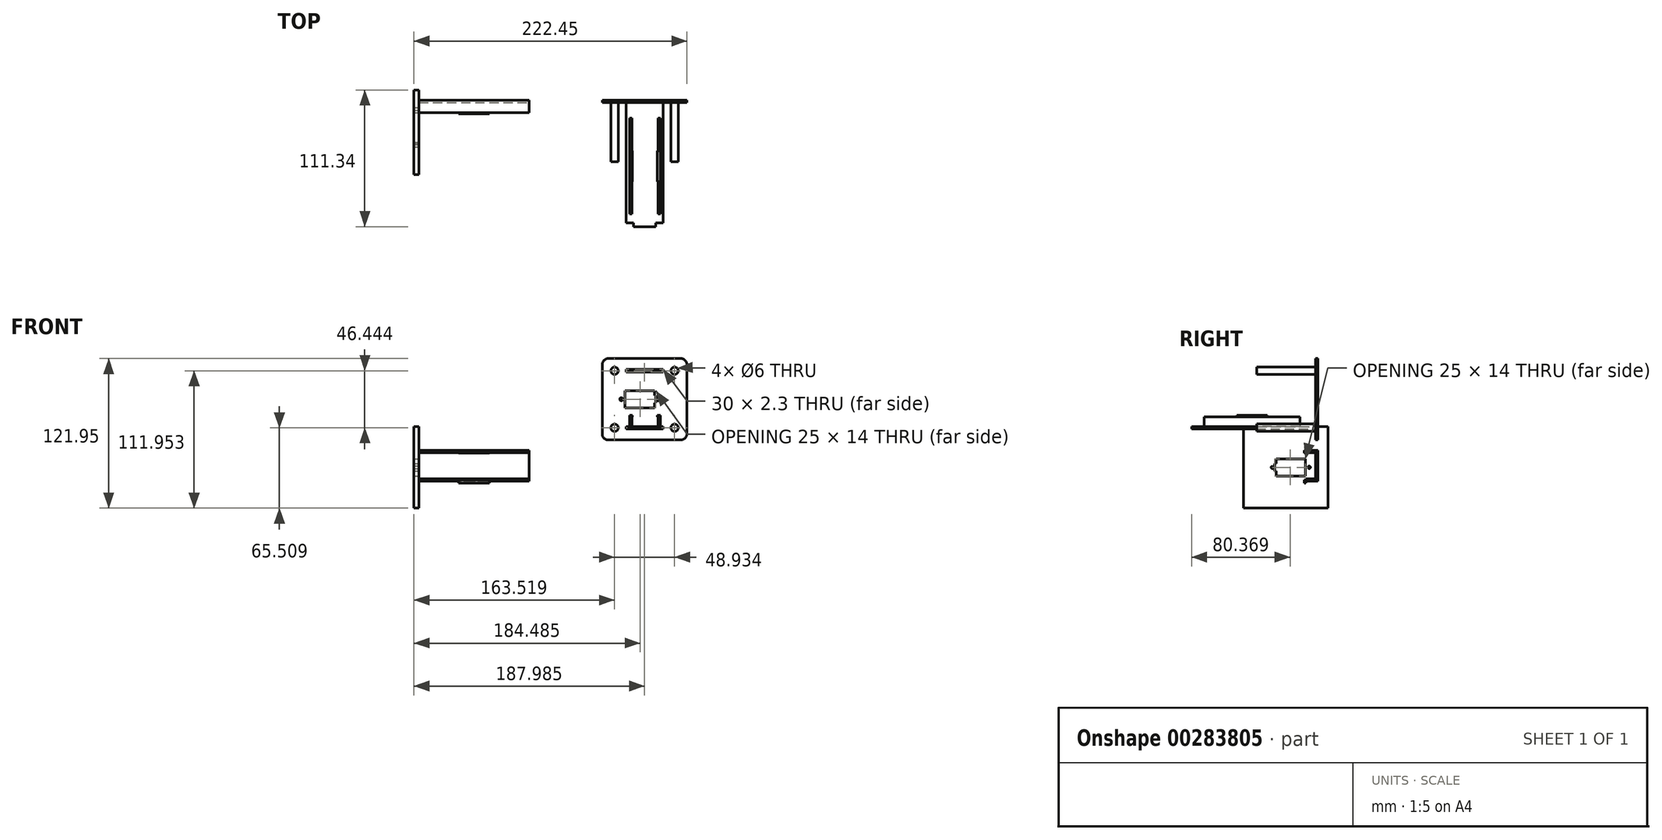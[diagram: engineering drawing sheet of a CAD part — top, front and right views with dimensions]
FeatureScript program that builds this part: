
annotation { "Feature Type Name" : "Feature", "Feature Type Description" : "" }
export const myFeature = defineFeature(function(context is Context, id is Id, definition is map)
    precondition{}
    {
        {
            var Q0;
            Q0=qCreatedBy(makeId("Front.planeOp"),FACE);
            var sketch = newSketch(context, id + "F0", { "sketchPlane" : qUnion([Q0])});
            skLineSegment(sketch, "E0.bottom", {"start": v(-132.32, 48.21) * mm, "end": v(-201.25, 48.21) * mm});
            skLineSegment(sketch, "E0.top", {"start": v(-132.32, -18.23) * mm, "end": v(-201.25, -18.23) * mm});
            skLineSegment(sketch, "E0.left", {"start": v(-132.32, 48.21) * mm, "end": v(-132.32, -18.23) * mm});
            skLineSegment(sketch, "E0.right", {"start": v(-201.25, 48.21) * mm, "end": v(-201.25, -18.23) * mm});
            skLineSegment(sketch, "E1.bottom", {"start": v(-158.78, 22) * mm, "end": v(-182.78, 22) * mm});
            skLineSegment(sketch, "E1.top", {"start": v(-158.78, 8) * mm, "end": v(-182.78, 8) * mm});
            skLineSegment(sketch, "E1.left", {"start": v(-158.78, 22) * mm, "end": v(-158.78, 8) * mm});
            skLineSegment(sketch, "E1.right", {"start": v(-182.78, 22) * mm, "end": v(-182.78, 8) * mm});
            skLineSegment(sketch, "E2.bottom", {"start": v(-157.78, 18) * mm, "end": v(-158.78, 18) * mm});
            skLineSegment(sketch, "E2.top", {"start": v(-157.78, 12) * mm, "end": v(-158.78, 12) * mm});
            skLineSegment(sketch, "E2.left", {"start": v(-157.78, 18) * mm, "end": v(-157.78, 12) * mm});
            skLineSegment(sketch, "E2.right", {"start": v(-158.78, 18) * mm, "end": v(-158.78, 12) * mm});
            skCircle(sketch, "E3", {"center": v(-155.78, 15) * mm, "radius": 1.25 * mm});
            skCircle(sketch, "E4", {"center": v(-185.78, 15) * mm, "radius": 1.25 * mm});
            skPoint(sketch, "E5", {"position": v(-182.78, 15) * mm});
            skPoint(sketch, "E6", {"position": v(-157.78, 15) * mm});
            skPoint(sketch, "E7", {"position": v(-158.78, 15) * mm});
            skPoint(sketch, "E8", {"position": v(-166.78, 48.21) * mm});
            skPoint(sketch, "E9", {"position": v(-132.32, 15) * mm});
            skPoint(sketch, "E10", {"position": v(-201.25, 15) * mm});
            skPoint(sketch, "E11", {"position": v(-166.78, -18.23) * mm});
            skLineSegment(sketch, "E12", {"start": v(-105.7, 15) * mm, "end": v(-235.07, 15) * mm, "construction": true});
            skPoint(sketch, "E13", {"position": v(-166.78, 22) * mm});
            skLineSegment(sketch, "E14.bottom", {"start": v(-350.77, -28.53) * mm, "end": v(-260.77, -28.53) * mm});
            skLineSegment(sketch, "E14.top", {"start": v(-350.77, -49.78) * mm, "end": v(-260.77, -49.78) * mm});
            skLineSegment(sketch, "E14.left", {"start": v(-350.77, -28.53) * mm, "end": v(-350.77, -49.78) * mm});
            skLineSegment(sketch, "E14.right", {"start": v(-260.77, -28.53) * mm, "end": v(-260.77, -49.78) * mm});
            skCircle(sketch, "E15", {"center": v(-191.25, 38.21) * mm, "radius": 3 * mm});
            skCircle(sketch, "E16", {"center": v(-142.32, 38.21) * mm, "radius": 3 * mm});
            skCircle(sketch, "E17", {"center": v(-142.32, -8.23) * mm, "radius": 3 * mm});
            skCircle(sketch, "E18", {"center": v(-191.25, -8.23) * mm, "radius": 3 * mm});
            skLineSegment(sketch, "E19.top", {"start": v(-350.77, -26.53) * mm, "end": v(-260.77, -26.53) * mm});
            skLineSegment(sketch, "E19.left", {"start": v(-350.77, -28.53) * mm, "end": v(-350.77, -26.53) * mm});
            skLineSegment(sketch, "E19.right", {"start": v(-260.77, -28.53) * mm, "end": v(-260.77, -26.53) * mm});
            skLineSegment(sketch, "E20.bottom", {"start": v(-260.77, -49.78) * mm, "end": v(-350.77, -49.78) * mm});
            skLineSegment(sketch, "E20.top", {"start": v(-260.77, -51.78) * mm, "end": v(-350.77, -51.78) * mm});
            skLineSegment(sketch, "E20.left", {"start": v(-260.77, -49.78) * mm, "end": v(-260.77, -51.78) * mm});
            skLineSegment(sketch, "E20.right", {"start": v(-350.77, -49.78) * mm, "end": v(-350.77, -51.78) * mm});
            skLineSegment(sketch, "E21.bottom", {"start": v(-151.78, 37.06) * mm, "end": v(-181.78, 37.06) * mm});
            skLineSegment(sketch, "E21.top", {"start": v(-151.78, 39.36) * mm, "end": v(-181.78, 39.36) * mm});
            skLineSegment(sketch, "E21.left", {"start": v(-151.78, 37.06) * mm, "end": v(-151.78, 39.36) * mm});
            skLineSegment(sketch, "E21.right", {"start": v(-181.78, 37.06) * mm, "end": v(-181.78, 39.36) * mm});
            skPoint(sketch, "E21.middle", {"position": v(-166.78, 38.21) * mm});
            skLineSegment(sketch, "E22.bottom", {"start": v(-181.78, -9.23) * mm, "end": v(-151.78, -9.23) * mm});
            skLineSegment(sketch, "E22.top", {"start": v(-181.78, -7.23) * mm, "end": v(-151.78, -7.23) * mm});
            skLineSegment(sketch, "E22.left", {"start": v(-181.78, -9.23) * mm, "end": v(-181.78, -7.23) * mm});
            skLineSegment(sketch, "E22.right", {"start": v(-151.78, -9.23) * mm, "end": v(-151.78, -7.23) * mm});
            skPoint(sketch, "E22.middle", {"position": v(-166.78, -8.23) * mm});
            skSolve(sketch);
        }
        {
            var Q0;
            Q0=makeQuery(id+"F0.imprint","IMPRINT",FACE,{"disambiguationData":[TD([[makeQuery(id+"F0.imprint","IMPRINT",EDGE,{"derivedFrom":sQuery(id+"F0.wireOp",EDGE,"E15")}),1.0]])]});
            var Q1;
            Q1=makeQuery(id+"F0.imprint","IMPRINT",FACE,{"disambiguationData":[TD([[makeQuery(id+"F0.imprint","IMPRINT",EDGE,{"derivedFrom":sQuery(id+"F0.wireOp",EDGE,"E16")}),1.0]])]});
            var Q2;
            Q2=makeQuery(id+"F0.imprint","IMPRINT",FACE,{"disambiguationData":[TD([[makeQuery(id+"F0.imprint","IMPRINT",EDGE,{"derivedFrom":sQuery(id+"F0.wireOp",EDGE,"E17")}),1.0]])]});
            var Q3;
            Q3=makeQuery(id+"F0.imprint","IMPRINT",FACE,{"disambiguationData":[TD([[makeQuery(id+"F0.imprint","IMPRINT",EDGE,{"derivedFrom":sQuery(id+"F0.wireOp",EDGE,"E18")}),1.0]])]});
            extrude(context, id + "F1", {"entities" : qUnion([Q0, Q1, Q2, Q3]), "depth" : 50 * mm});
        }
        {
            var Q0;
            Q0=makeQuery(id+"F0.imprint","IMPRINT",FACE,{"disambiguationData":[TD([[makeQuery(id+"F0.imprint","IMPRINT",EDGE,{"derivedFrom":sQuery(id+"F0.wireOp",EDGE,"E0.bottom")}),1.0]])]});
            extrude(context, id + "F2", {"entities" : qUnion([Q0]), "depth" : 2 * mm});
        }
        {
            var Q0;
            Q0=makeQuery(id+"F0.imprint","IMPRINT",FACE,{"disambiguationData":[TD([[makeQuery(id+"F0.imprint","IMPRINT",EDGE,{"derivedFrom":sQuery(id+"F0.wireOp",EDGE,"E14.bottom")}),1.0]])]});
            var Q1;
            Q1=makeQuery(id+"F0.imprint","IMPRINT",FACE,{"disambiguationData":[TD([[makeQuery(id+"F0.imprint","IMPRINT",EDGE,{"derivedFrom":sQuery(id+"F0.wireOp",EDGE,"E14.top")}),-1.0]])]});
            extrude(context, id + "F3", {"entities" : qUnion([Q0, Q1]), "offsetDistance" : 25 * mm, "depth" : 10 * mm});
        }
        {
            var Q0;
            Q0=makeQuery(id+"F0.imprint","IMPRINT",FACE,{"disambiguationData":[TD([[makeQuery(id+"F0.imprint","IMPRINT",EDGE,{"derivedFrom":sQuery(id+"F0.wireOp",EDGE,"E14.bottom")}),-1.0]])]});
            extrude(context, id + "F4", {"entities" : qUnion([Q0]), "depth" : 2 * mm});
        }
        {
            var Q0;
            Q0=makeQuery(id+"F3.opExtrude","CAP_FACE",FACE,{"disambiguationData":[OSD([sQuery(id+"F0.wireOp",EDGE,"E14.bottom"),sQuery(id+"F0.wireOp",EDGE,"E19.top"),sQuery(id+"F0.wireOp",EDGE,"E19.left"),sQuery(id+"F0.wireOp",EDGE,"E19.right")])],"isStart":false});
            var sketch = newSketch(context, id + "F5", { "sketchPlane" : qUnion([Q0])});
            skLineSegment(sketch, "E23.bottom", {"start": v(-318.27, -26.53) * mm, "end": v(-293.27, -26.53) * mm});
            skLineSegment(sketch, "E23.top", {"start": v(-318.27, -29.03) * mm, "end": v(-293.27, -29.03) * mm});
            skLineSegment(sketch, "E23.left", {"start": v(-318.27, -26.53) * mm, "end": v(-318.27, -29.03) * mm});
            skLineSegment(sketch, "E23.right", {"start": v(-293.27, -26.53) * mm, "end": v(-293.27, -29.03) * mm});
            skLineSegment(sketch, "E24.bottom", {"start": v(-318.27, -50.8) * mm, "end": v(-293.27, -50.8) * mm});
            skLineSegment(sketch, "E24.top", {"start": v(-318.27, -53.3) * mm, "end": v(-293.27, -53.3) * mm});
            skLineSegment(sketch, "E24.left", {"start": v(-318.27, -50.8) * mm, "end": v(-318.27, -53.3) * mm});
            skLineSegment(sketch, "E24.right", {"start": v(-293.27, -50.8) * mm, "end": v(-293.27, -53.3) * mm});
            skPoint(sketch, "E25", {"position": v(-305.77, -53.3) * mm});
            skPoint(sketch, "E26", {"position": v(-305.77, -26.53) * mm});
            skSolve(sketch);
        }
        {
            var Q0;
            Q0 = qSketchRegion(id + "F5", true);
            extrude(context, id + "F6", {"entities" : qUnion([Q0]), "depth" : 1 * mm});
        }
        {
            var Q0;
            Q0=makeQuery(id+"F2.opExtrude","SWEPT_EDGE",EDGE,{"disambiguationData":[OSD([sQuery(id+"F0.wireOp",EDGE,"E0.bottom"),sQuery(id+"F0.wireOp",EDGE,"E0.right")])]});
            var Q1;
            Q1=makeQuery(id+"F2.opExtrude","SWEPT_EDGE",EDGE,{"disambiguationData":[OSD([sQuery(id+"F0.wireOp",EDGE,"E0.bottom"),sQuery(id+"F0.wireOp",EDGE,"E0.left")])]});
            var Q2;
            Q2=makeQuery(id+"F2.opExtrude","SWEPT_EDGE",EDGE,{"disambiguationData":[OSD([sQuery(id+"F0.wireOp",EDGE,"E0.top"),sQuery(id+"F0.wireOp",EDGE,"E0.left")])]});
            var Q3;
            Q3=makeQuery(id+"F2.opExtrude","SWEPT_EDGE",EDGE,{"disambiguationData":[OSD([sQuery(id+"F0.wireOp",EDGE,"E0.top"),sQuery(id+"F0.wireOp",EDGE,"E0.right")])]});
            fillet(context, id + "F7", {"entities" : qUnion([Q0, Q1, Q2, Q3]), "radius" : 5 * mm, "tangentPropagation" : true, "allowEdgeOverflow" : false});
        }
        {
            var Q0;
            Q0=makeQuery(id+"F4.opExtrude","SWEPT_FACE",FACE,{"disambiguationData":[OSD([sQuery(id+"F0.wireOp",EDGE,"E14.left")])]});
            var sketch = newSketch(context, id + "F8", { "sketchPlane" : qUnion([Q0])});
            skLineSegment(sketch, "E27.bottom", {"start": v(60.6, -7.3) * mm, "end": v(-8.34, -7.3) * mm});
            skLineSegment(sketch, "E27.top", {"start": v(60.6, -73.74) * mm, "end": v(-8.34, -73.74) * mm});
            skLineSegment(sketch, "E27.left", {"start": v(60.6, -7.3) * mm, "end": v(60.6, -73.74) * mm});
            skLineSegment(sketch, "E27.right", {"start": v(-8.34, -7.3) * mm, "end": v(-8.34, -73.74) * mm});
            skLineSegment(sketch, "E28.bottom", {"start": v(34.13, -33.51) * mm, "end": v(10.13, -33.51) * mm});
            skLineSegment(sketch, "E28.top", {"start": v(34.13, -47.51) * mm, "end": v(10.13, -47.51) * mm});
            skLineSegment(sketch, "E28.left", {"start": v(34.13, -33.51) * mm, "end": v(34.13, -47.51) * mm});
            skLineSegment(sketch, "E28.right", {"start": v(10.13, -33.51) * mm, "end": v(10.13, -47.51) * mm});
            skLineSegment(sketch, "E29.bottom", {"start": v(35.13, -37.51) * mm, "end": v(34.13, -37.51) * mm});
            skLineSegment(sketch, "E29.top", {"start": v(35.13, -43.51) * mm, "end": v(34.13, -43.51) * mm});
            skLineSegment(sketch, "E29.left", {"start": v(35.13, -37.51) * mm, "end": v(35.13, -43.51) * mm});
            skLineSegment(sketch, "E29.right", {"start": v(34.13, -37.51) * mm, "end": v(34.13, -43.51) * mm});
            skCircle(sketch, "E30", {"center": v(37.13, -40.51) * mm, "radius": 1 * mm});
            skCircle(sketch, "E31", {"center": v(7.13, -40.51) * mm, "radius": 1 * mm});
            skPoint(sketch, "E32", {"position": v(10.13, -40.51) * mm});
            skPoint(sketch, "E33", {"position": v(35.13, -40.51) * mm});
            skPoint(sketch, "E34", {"position": v(34.13, -40.51) * mm});
            skPoint(sketch, "E35", {"position": v(26.13, -7.3) * mm});
            skPoint(sketch, "E36", {"position": v(60.6, -40.51) * mm});
            skPoint(sketch, "E37", {"position": v(-8.34, -40.51) * mm});
            skPoint(sketch, "E38", {"position": v(26.13, -73.74) * mm});
            skLineSegment(sketch, "E39", {"start": v(26.13, 20.06) * mm, "end": v(26.13, -87.09) * mm, "construction": true});
            skLineSegment(sketch, "E40", {"start": v(61.84, -40.51) * mm, "end": v(-35.9, -40.51) * mm, "construction": true});
            skPoint(sketch, "E41", {"position": v(26.13, -33.51) * mm});
            skPoint(sketch, "E42", {"position": v(0, -39.15) * mm});
            skSolve(sketch);
        }
        {
            var Q0;
            {var subQ5=sQuery(id+"F0.wireOp",EDGE,"E14.left");var subQ8=makeQuery(id+"F8.imprint","IMPRINT",EDGE,{"derivedFrom":makeQuery(id+"F4.opExtrude","CAP_EDGE",EDGE,{"disambiguationData":[OSD([subQ5])],"isStart":true})});Q0=qUnion([makeQuery(id+"F8.imprint","IMPRINT",FACE,{"disambiguationData":[TD([[subQ8,1.0]])]}),makeQuery(id+"F8.imprint","IMPRINT",FACE,{"disambiguationData":[TD([[makeQuery(id+"F8.imprint","IMPRINT",EDGE,{"derivedFrom":sQuery(id+"F8.wireOp",EDGE,"E27.bottom")}),1.0]])]})]);}
            extrude(context, id + "F9", {"entities" : qUnion([Q0]), "depth" : 4 * mm});
        }
        {
            var Q0;
            Q0=makeQuery(id+"F0.imprint","IMPRINT",FACE,{"disambiguationData":[TD([[makeQuery(id+"F0.imprint","IMPRINT",EDGE,{"derivedFrom":sQuery(id+"F0.wireOp",EDGE,"E22.bottom")}),1.0]])]});
            extrude(context, id + "F10", {"entities" : qUnion([Q0]), "operationType" : NewBodyOperationType.ADD, "depth" : 100 * mm});
        }
        {
            var Q0;
            Q0=makeQuery(id+"F10.opExtrude","SWEPT_FACE",FACE,{"disambiguationData":[OSD([sQuery(id+"F0.wireOp",EDGE,"E22.top")])]});
            var sketch = newSketch(context, id + "F11", { "sketchPlane" : qUnion([Q0])});
            skLineSegment(sketch, "E43.bottom", {"start": v(-155.83, -92.7) * mm, "end": v(-177.08, -92.7) * mm});
            skLineSegment(sketch, "E43.top", {"start": v(-155.83, -14.7) * mm, "end": v(-177.08, -14.7) * mm});
            skLineSegment(sketch, "E43.left", {"start": v(-155.83, -92.7) * mm, "end": v(-155.83, -14.7) * mm});
            skLineSegment(sketch, "E43.right", {"start": v(-177.08, -92.7) * mm, "end": v(-177.08, -14.7) * mm});
            skPoint(sketch, "E43.middle", {"position": v(-166.46, -53.7) * mm});
            skLineSegment(sketch, "E44.bottom", {"start": v(-155.83, -14.7) * mm, "end": v(-153.83, -14.7) * mm});
            skLineSegment(sketch, "E44.top", {"start": v(-155.83, -92.7) * mm, "end": v(-153.83, -92.7) * mm});
            skLineSegment(sketch, "E44.left", {"start": v(-155.83, -14.7) * mm, "end": v(-155.83, -92.7) * mm});
            skLineSegment(sketch, "E44.right", {"start": v(-153.83, -14.7) * mm, "end": v(-153.83, -92.7) * mm});
            skLineSegment(sketch, "E45.bottom", {"start": v(-177.08, -14.7) * mm, "end": v(-179.08, -14.7) * mm});
            skLineSegment(sketch, "E45.top", {"start": v(-177.08, -92.7) * mm, "end": v(-179.08, -92.7) * mm});
            skLineSegment(sketch, "E45.left", {"start": v(-177.08, -14.7) * mm, "end": v(-177.08, -92.7) * mm});
            skLineSegment(sketch, "E45.right", {"start": v(-179.08, -14.7) * mm, "end": v(-179.08, -92.7) * mm});
            skSolve(sketch);
        }
        {
            var Q0;
            Q0=makeQuery(id+"F11.imprint","IMPRINT",FACE,{"disambiguationData":[TD([[makeQuery(id+"F11.imprint","IMPRINT",EDGE,{"derivedFrom":sQuery(id+"F11.wireOp",EDGE,"E45.bottom")}),1.0]])]});
            var Q1;
            Q1=makeQuery(id+"F11.imprint","IMPRINT",FACE,{"disambiguationData":[TD([[makeQuery(id+"F11.imprint","IMPRINT",EDGE,{"derivedFrom":sQuery(id+"F11.wireOp",EDGE,"E44.bottom")}),-1.0]])]});
            extrude(context, id + "F12", {"entities" : qUnion([Q0, Q1]), "operationType" : NewBodyOperationType.ADD, "depth" : 8 * mm});
        }
        {
            var Q0;
            Q0=makeQuery(id+"F12.opExtrude","CAP_FACE",FACE,{"disambiguationData":[OSD([sQuery(id+"F11.wireOp",EDGE,"E45.bottom"),sQuery(id+"F11.wireOp",EDGE,"E45.top"),sQuery(id+"F11.wireOp",EDGE,"E45.left"),sQuery(id+"F11.wireOp",EDGE,"E45.right")])],"isStart":false});
            var sketch = newSketch(context, id + "F13", { "sketchPlane" : qUnion([Q0])});
            skPoint(sketch, "E46", {"position": v(-179.08, -53.7) * mm});
            skLineSegment(sketch, "E47.bottom", {"start": v(-179.08, -41.2) * mm, "end": v(-176.58, -41.2) * mm});
            skLineSegment(sketch, "E47.top", {"start": v(-179.08, -66.2) * mm, "end": v(-176.58, -66.2) * mm});
            skLineSegment(sketch, "E47.left", {"start": v(-179.08, -41.2) * mm, "end": v(-179.08, -66.2) * mm});
            skLineSegment(sketch, "E47.right", {"start": v(-176.58, -41.2) * mm, "end": v(-176.58, -66.2) * mm});
            skLineSegment(sketch, "E48.bottom", {"start": v(-153.92, -41.2) * mm, "end": v(-156.42, -41.2) * mm});
            skLineSegment(sketch, "E48.top", {"start": v(-153.92, -66.2) * mm, "end": v(-156.42, -66.2) * mm});
            skLineSegment(sketch, "E48.left", {"start": v(-153.92, -41.2) * mm, "end": v(-153.92, -66.2) * mm});
            skLineSegment(sketch, "E48.right", {"start": v(-156.42, -41.2) * mm, "end": v(-156.42, -66.2) * mm});
            skPoint(sketch, "E49", {"position": v(-176.58, -53.7) * mm});
            skPoint(sketch, "E50", {"position": v(-156.42, -53.7) * mm});
            skPoint(sketch, "E51", {"position": v(-156.14, -53.7) * mm});
            skPoint(sketch, "E51.positionSnap0", {"position": v(-153.92, -53.7) * mm});
            skSolve(sketch);
        }
        {
            var Q0;
            Q0 = qSketchRegion(id + "F13", true);
            extrude(context, id + "F14", {"entities" : qUnion([Q0]), "operationType" : NewBodyOperationType.ADD, "depth" : 1 * mm});
        }
        {
            var Q0;
            Q0=makeQuery(id+"F10.opExtrude","CAP_FACE",FACE,{"disambiguationData":[OSD([sQuery(id+"F0.wireOp",EDGE,"E22.bottom"),sQuery(id+"F0.wireOp",EDGE,"E22.top"),sQuery(id+"F0.wireOp",EDGE,"E22.left"),sQuery(id+"F0.wireOp",EDGE,"E22.right")])],"isStart":false});
            var sketch = newSketch(context, id + "F15", { "sketchPlane" : qUnion([Q0])});
            skLineSegment(sketch, "E52.bottom", {"start": v(-175.78, -7.23) * mm, "end": v(-157.78, -7.23) * mm});
            skLineSegment(sketch, "E52.top", {"start": v(-175.78, -9.23) * mm, "end": v(-157.78, -9.23) * mm});
            skLineSegment(sketch, "E52.left", {"start": v(-175.78, -7.23) * mm, "end": v(-175.78, -9.23) * mm});
            skLineSegment(sketch, "E52.right", {"start": v(-157.78, -7.23) * mm, "end": v(-157.78, -9.23) * mm});
            skPoint(sketch, "E53", {"position": v(-166.78, -9.23) * mm});
            skSolve(sketch);
        }
        {
            var Q0;
            Q0=makeQuery(id+"F15.imprint","IMPRINT",FACE,{"disambiguationData":[TD([[makeQuery(id+"F15.imprint","IMPRINT",EDGE,{"derivedFrom":sQuery(id+"F15.wireOp",EDGE,"E52.bottom")}),-1.0]])]});
            extrude(context, id + "F16", {"entities" : qUnion([Q0]), "operationType" : NewBodyOperationType.ADD, "depth" : 3 * mm});
        }
    });
